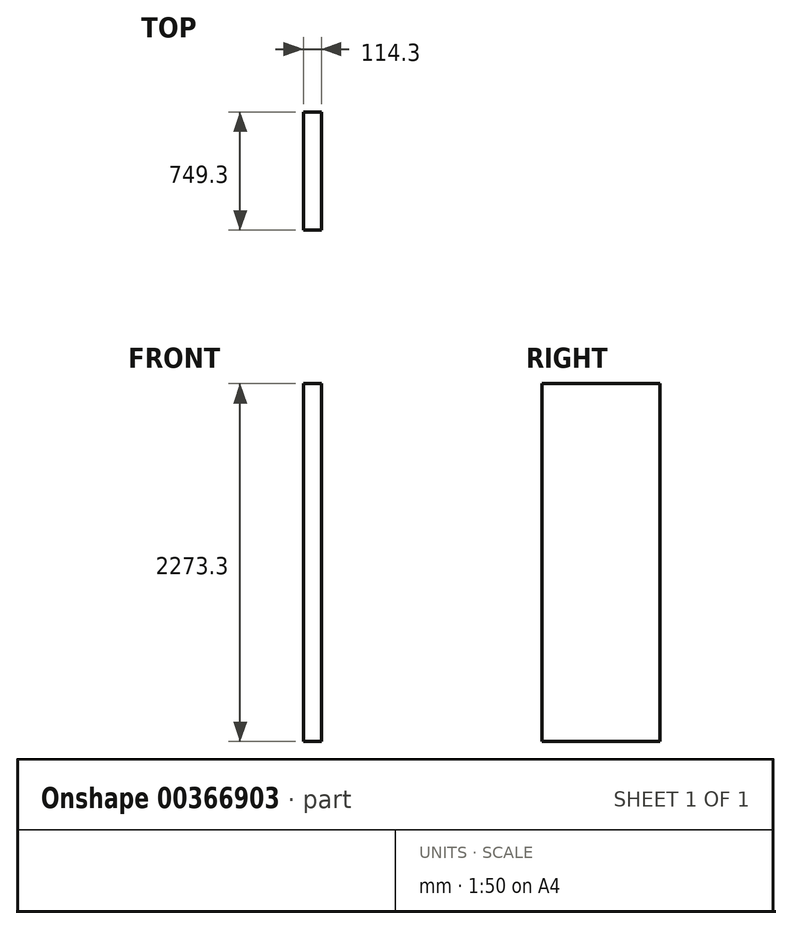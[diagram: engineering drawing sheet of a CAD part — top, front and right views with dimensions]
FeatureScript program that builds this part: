
annotation { "Feature Type Name" : "Feature", "Feature Type Description" : "" }
export const myFeature = defineFeature(function(context is Context, id is Id, definition is map)
    precondition{}
    {
        {
            var Q0;
            Q0=qCreatedBy(makeId("Right.planeOp"),FACE);
            var sketch = newSketch(context, id + "F0", { "sketchPlane" : qUnion([Q0])});
            skLineSegment(sketch, "E0.bottom", {"start": v(0, 0) * mm, "end": v(-749.3, 0) * mm});
            skLineSegment(sketch, "E0.top", {"start": v(0, 2273.3) * mm, "end": v(-749.3, 2273.3) * mm});
            skLineSegment(sketch, "E0.left", {"start": v(0, 0) * mm, "end": v(0, 2273.3) * mm});
            skLineSegment(sketch, "E0.right", {"start": v(-749.3, 0) * mm, "end": v(-749.3, 2273.3) * mm});
            skSolve(sketch);
        }
        {
            var Q0;
            Q0 = qSketchRegion(id + "F0", true);
            extrude(context, id + "F1", {"entities" : qUnion([Q0]), "depth" : 114.3 * mm});
        }
    });
